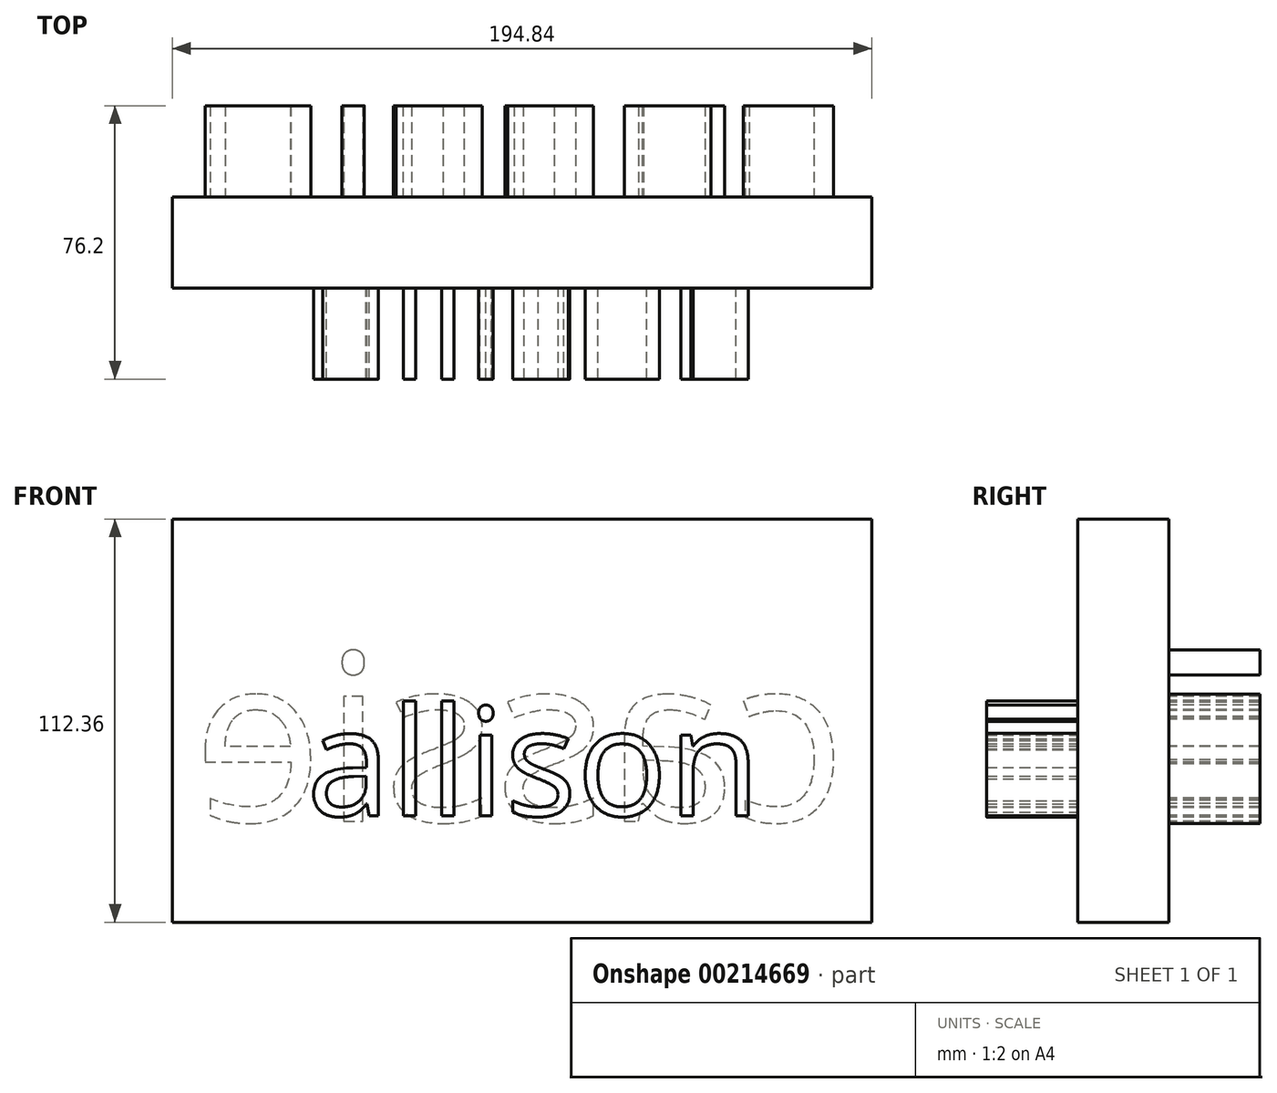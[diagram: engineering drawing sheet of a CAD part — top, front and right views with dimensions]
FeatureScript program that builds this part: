
annotation { "Feature Type Name" : "Feature", "Feature Type Description" : "" }
export const myFeature = defineFeature(function(context is Context, id is Id, definition is map)
    precondition{}
    {
        {
            var Q0;
            Q0=qCreatedBy(makeId("Front.planeOp"),FACE);
            var sketch = newSketch(context, id + "F0", { "sketchPlane" : qUnion([Q0])});
            skLineSegment(sketch, "E0.bottom", {"start": v(-102.62, 65.71) * mm, "end": v(92.22, 65.71) * mm});
            skLineSegment(sketch, "E0.top", {"start": v(-102.62, -46.65) * mm, "end": v(92.22, -46.65) * mm});
            skLineSegment(sketch, "E0.left", {"start": v(-102.62, 65.71) * mm, "end": v(-102.62, -46.65) * mm});
            skLineSegment(sketch, "E0.right", {"start": v(92.22, 65.71) * mm, "end": v(92.22, -46.65) * mm});
            skSolve(sketch);
        }
        {
            var Q0;
            Q0 = qSketchRegion(id + "F0", true);
            extrude(context, id + "F1", {"entities" : qUnion([Q0]), "depth" : 25.4 * mm});
        }
        {
            var Q0;
            Q0=makeQuery(id+"F1.opExtrude","CAP_FACE",FACE,{"disambiguationData":[OSD([sQuery(id+"F0.wireOp",EDGE,"E0.bottom"),sQuery(id+"F0.wireOp",EDGE,"E0.top"),sQuery(id+"F0.wireOp",EDGE,"E0.left"),sQuery(id+"F0.wireOp",EDGE,"E0.right")])],"isStart":false});
            var sketch = newSketch(context, id + "F2", { "sketchPlane" : qUnion([Q0])});
            skText(sketch, "E1", { "text": "allison", "fontName": "OpenSans-Regular.ttf"});
            const initialGuessF2  = {"E1": [-0.06522, -0.01694, 1, 0, 0.03024]};
            skSetInitialGuess(sketch, initialGuessF2);
            skSolve(sketch);
        }
        {
            var Q0;
            Q0 = qSketchRegion(id + "F2", true);
            extrude(context, id + "F3", {"entities" : qUnion([Q0]), "operationType" : NewBodyOperationType.ADD, "depth" : 25.4 * mm});
        }
        {
            var Q0;
            Q0=makeQuery(id+"F1.opExtrude","CAP_FACE",FACE,{"disambiguationData":[OSD([sQuery(id+"F0.wireOp",EDGE,"E0.bottom"),sQuery(id+"F0.wireOp",EDGE,"E0.top"),sQuery(id+"F0.wireOp",EDGE,"E0.left"),sQuery(id+"F0.wireOp",EDGE,"E0.right")])],"isStart":true});
            var sketch = newSketch(context, id + "F4", { "sketchPlane" : qUnion([Q0])});
            skText(sketch, "E2", { "text": "cassie", "fontName": "OpenSans-Regular.ttf"});
            const initialGuessF4  = {"E2": [-0.08527, -0.01848, 1, 0, 0.04686]};
            skSetInitialGuess(sketch, initialGuessF4);
            skSolve(sketch);
        }
        {
            var Q0;
            Q0 = qSketchRegion(id + "F4", true);
            extrude(context, id + "F5", {"entities" : qUnion([Q0]), "operationType" : NewBodyOperationType.ADD, "depth" : 25.4 * mm});
        }
    });
